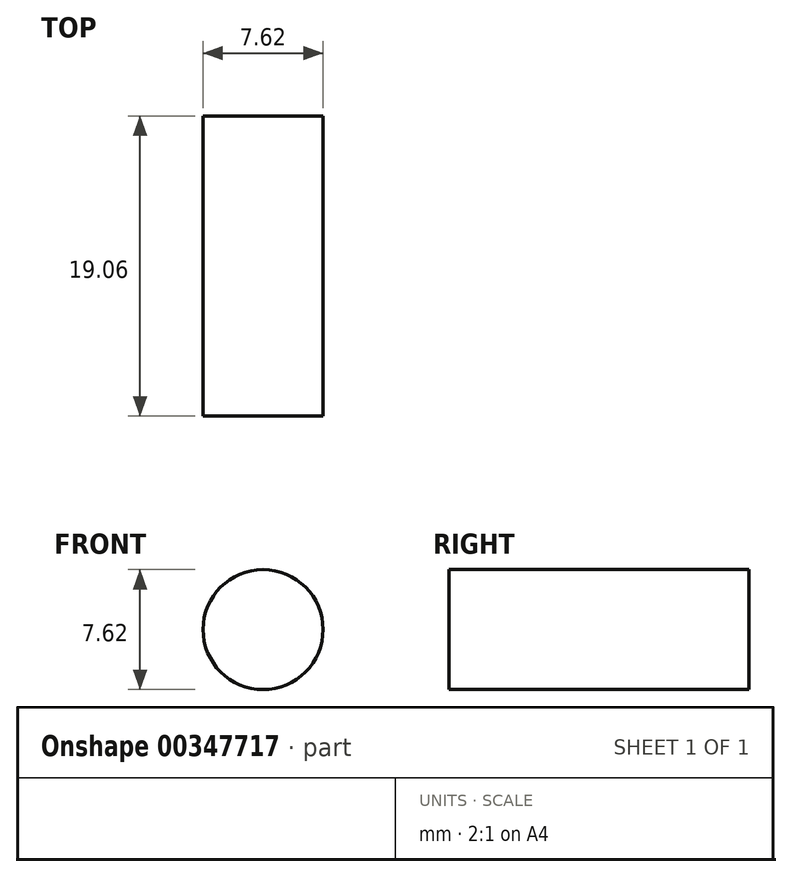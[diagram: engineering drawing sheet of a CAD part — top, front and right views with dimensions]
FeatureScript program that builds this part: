
annotation { "Feature Type Name" : "Feature", "Feature Type Description" : "" }
export const myFeature = defineFeature(function(context is Context, id is Id, definition is map)
    precondition{}
    {
        {
            var Q0;
            Q0=qCreatedBy(makeId("Front.planeOp"),FACE);
            var sketch = newSketch(context, id + "F0", { "sketchPlane" : qUnion([Q0])});
            skCircle(sketch, "E0", {"center": v(0, 0) * mm, "radius": 3.81 * mm});
            skSolve(sketch);
        }
        {
            var Q0;
            Q0=makeQuery(id+"F0.imprint","IMPRINT",FACE,{"disambiguationData":[TD([[makeQuery(id+"F0.imprint","IMPRINT",EDGE,{"derivedFrom":sQuery(id+"F0.wireOp",EDGE,"E0")}),1.0]])]});
            extrude(context, id + "F1", {"entities" : qUnion([Q0]), "endBound" : BoundingType.SYMMETRIC, "depth" : 19.05 * mm});
        }
    });
